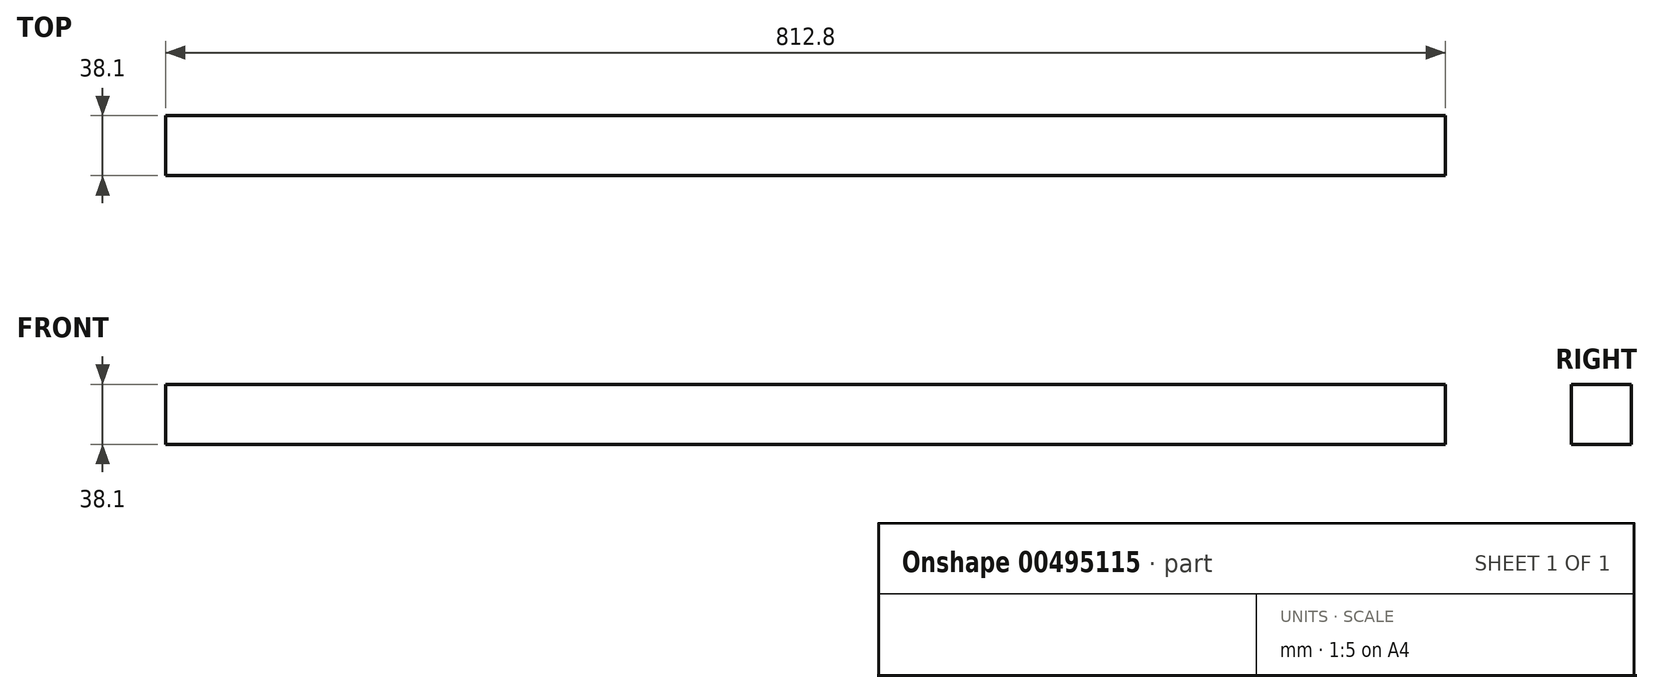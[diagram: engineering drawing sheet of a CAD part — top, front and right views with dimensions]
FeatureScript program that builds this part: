
annotation { "Feature Type Name" : "Feature", "Feature Type Description" : "" }
export const myFeature = defineFeature(function(context is Context, id is Id, definition is map)
    precondition{}
    {
        {
            var Q0;
            Q0=qCreatedBy(makeId("Front.planeOp"),FACE);
            var sketch = newSketch(context, id + "F0", { "sketchPlane" : qUnion([Q0])});
            skLineSegment(sketch, "E0.bottom", {"start": v(0, 0) * mm, "end": v(-812.8, 0) * mm});
            skLineSegment(sketch, "E0.top", {"start": v(0, 38.1) * mm, "end": v(-812.8, 38.1) * mm});
            skLineSegment(sketch, "E0.left", {"start": v(0, 0) * mm, "end": v(0, 38.1) * mm});
            skLineSegment(sketch, "E0.right", {"start": v(-812.8, 0) * mm, "end": v(-812.8, 38.1) * mm});
            skSolve(sketch);
        }
        {
            var Q0;
            Q0=makeQuery(id+"F0.imprint","IMPRINT",FACE,{"disambiguationData":[TD([[makeQuery(id+"F0.imprint","IMPRINT",EDGE,{"derivedFrom":sQuery(id+"F0.wireOp",EDGE,"E0.bottom")}),-1.0]])]});
            extrude(context, id + "F1", {"entities" : qUnion([Q0]), "depth" : 38.1 * mm});
        }
    });
